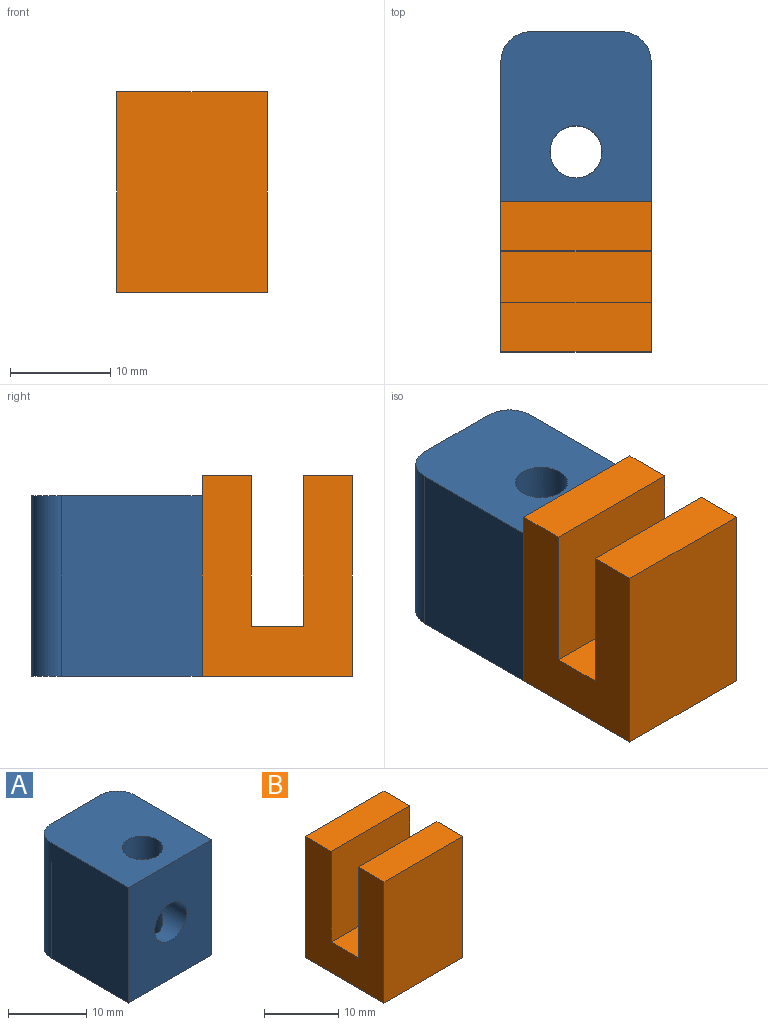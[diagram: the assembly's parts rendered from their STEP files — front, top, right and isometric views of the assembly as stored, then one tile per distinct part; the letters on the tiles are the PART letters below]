
ASSEMBLY  parts=2 mates=1
PART A: 11 faces, bbox 15x17x18 mm
  f0: cylinder r=2.6mm len=8.04mm, axis (0,0,-1), area 113.3mm2, adj f6,f10
  f1: cylinder r=2.6mm len=7.84mm, axis (0,0,-1), area 110mm2, adj f7,f10
  f2: plane 18x9mm, normal (0,1,0), area 135.6mm2, adj f6,f7,f8,f9,f10
  f3: plane 18x14mm, normal (-1,0,0), area 252mm2, adj f4,f6,f7,f8
  f4: plane 18x15mm, normal (0,-1,0), area 243.6mm2, adj f3,f5,f6,f7,f10
  f5: plane 18x14mm, normal (1,0,0), area 252mm2, adj f4,f6,f7,f9
  f6: plane 17x15mm, normal (0,0,1), area 229.9mm2, adj f0,f2,f3,f4,f5,f8,f9
  f7: plane 17x15mm, normal (0,0,-1), area 229.9mm2, adj f1,f2,f3,f4,f5,f8,f9
  f8: cylinder r=3mm len=18mm, axis (0,0,1), area 84.8mm2, adj f2,f3,f6,f7
  f9: cylinder r=3mm len=18mm, axis (0,0,-1), area 84.8mm2, adj f2,f5,f6,f7
  f10: cylinder r=2.9mm len=17mm, axis (0,1,0), area 260.4mm2, adj f0,f1,f2,f4
PART B: 10 faces, bbox 15x15x20 mm
  f0: plane 15x4.9mm, normal (0,0,1), area 73.5mm2, adj f1,f2,f6,f9
  f1: plane 20x15mm, normal (1,0,0), area 222mm2, adj f0,f2,f3,f4,f5,f6,f7,f8
  f2: plane 20x15mm, normal (0,1,0), area 300mm2, adj f0,f1,f5,f9
  f3: plane 20x15mm, normal (0,-1,0), area 300mm2, adj f1,f4,f5,f9
  f4: plane 15x4.9mm, normal (0,0,1), area 73.5mm2, adj f1,f3,f7,f9
  f5: plane 15x15mm, normal (0,0,-1), area 225mm2, adj f1,f2,f3,f9
  f6: plane 15x15mm, normal (0,-1,0), area 225mm2, adj f0,f1,f8,f9
  f7: plane 15x15mm, normal (0,1,0), area 225mm2, adj f1,f4,f8,f9
  f8: plane 15x5.2mm, normal (0,0,1), area 78mm2, adj f1,f6,f7,f9
  f9: plane 20x15mm, normal (-1,0,0), area 222mm2, adj f0,f2,f3,f4,f5,f6,f7,f8
PLACE A t=(-26.65,-44,-25.76)mm
PLACE B t=(-51.23,-43.13,-25.76)mm
MATE fastened A.f4 <-> B.f2  axis (0,-1,0) through (9.14,-4.87,-25.76)mm
